# Revit family: Window-2500_UT_Unitwall_System-GLASSvent-1in_Infill
name_source: partatom
category: Windows
revit_build: Autodesk Revit 2015 (Build: 20140606_1530(x64)
units: mm (PartAtom-declared; Revit-internal decimal feet)

## types (2) — shared parameters
Analytic Construction = <None>
Description = Window for Curtain Wall
Frame = Aluminum - Kawneer - Permafluor - Classic Bronze
Glazing = Glass
Manufacturer = Kawneer
Model = GLASSvent™ UT Window
Offset = 0' - 0"
Product Documentation Link = http://www.kawneer.com
Product Name = GLASSvent UT(Ultra Thermal) Windows 1in Infill
Product Page URL = http://www.kawneer.com
Product data url = https://bimobject.com
URL = www.kawneer.com

## per-type parameters (varying)
| type | Operation | Project Out |
| Project-Out | Project Out | Yes |
| Outswing Casement | Outswing Casement | No |

type visibility flags (boolean, named after types; folded from table):
- Project-Out: Yes: (none)
- Outswing Casement: Yes: Outswing Casement

## geometry (parser evidence)
native form markers: Blend x25, Sweep x7
no freeform markers — native parametric forms only
